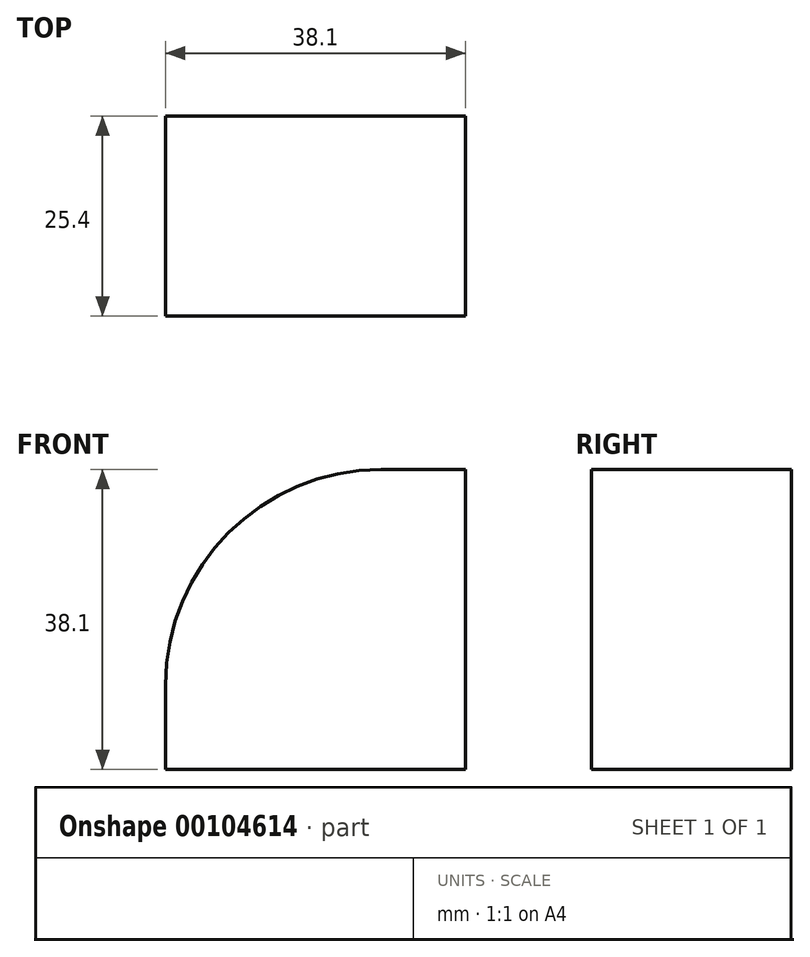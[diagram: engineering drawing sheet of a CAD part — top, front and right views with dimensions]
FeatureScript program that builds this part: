
annotation { "Feature Type Name" : "Feature", "Feature Type Description" : "" }
export const myFeature = defineFeature(function(context is Context, id is Id, definition is map)
    precondition{}
    {
        {
            var Q0;
            Q0=qCreatedBy(makeId("Front.planeOp"),FACE);
            var sketch = newSketch(context, id + "F0", { "sketchPlane" : qUnion([Q0])});
            skLineSegment(sketch, "E0.bottom", {"start": v(-18.57, 26.93) * mm, "end": v(-7.87, 26.93) * mm});
            skLineSegment(sketch, "E0.top", {"start": v(-45.97, -11.17) * mm, "end": v(-7.87, -11.17) * mm});
            skLineSegment(sketch, "E0.left", {"start": v(-45.97, -0.47) * mm, "end": v(-45.97, -11.17) * mm});
            skLineSegment(sketch, "E0.right", {"start": v(-7.87, 26.93) * mm, "end": v(-7.87, -11.17) * mm});
            skPoint(sketch, "E1.visualSharp", {"position": v(-45.97, 26.93) * mm});
            skArc(sketch, "E1.filletArc", {"start": v(-18.57, 26.93) * mm, "mid": v(-37.95, 18.9) * mm, "end": v(-45.97, -0.47) * mm});
            skSolve(sketch);
        }
        {
            var Q0;
            Q0=makeQuery(id+"F0.imprint","IMPRINT",FACE,{"disambiguationData":[TD([[makeQuery(id+"F0.imprint","IMPRINT",EDGE,{"derivedFrom":sQuery(id+"F0.wireOp",EDGE,"E0.bottom")}),-1.0]])]});
            extrude(context, id + "F1", {"entities" : qUnion([Q0]), "depth" : 25.4 * mm});
        }
    });
